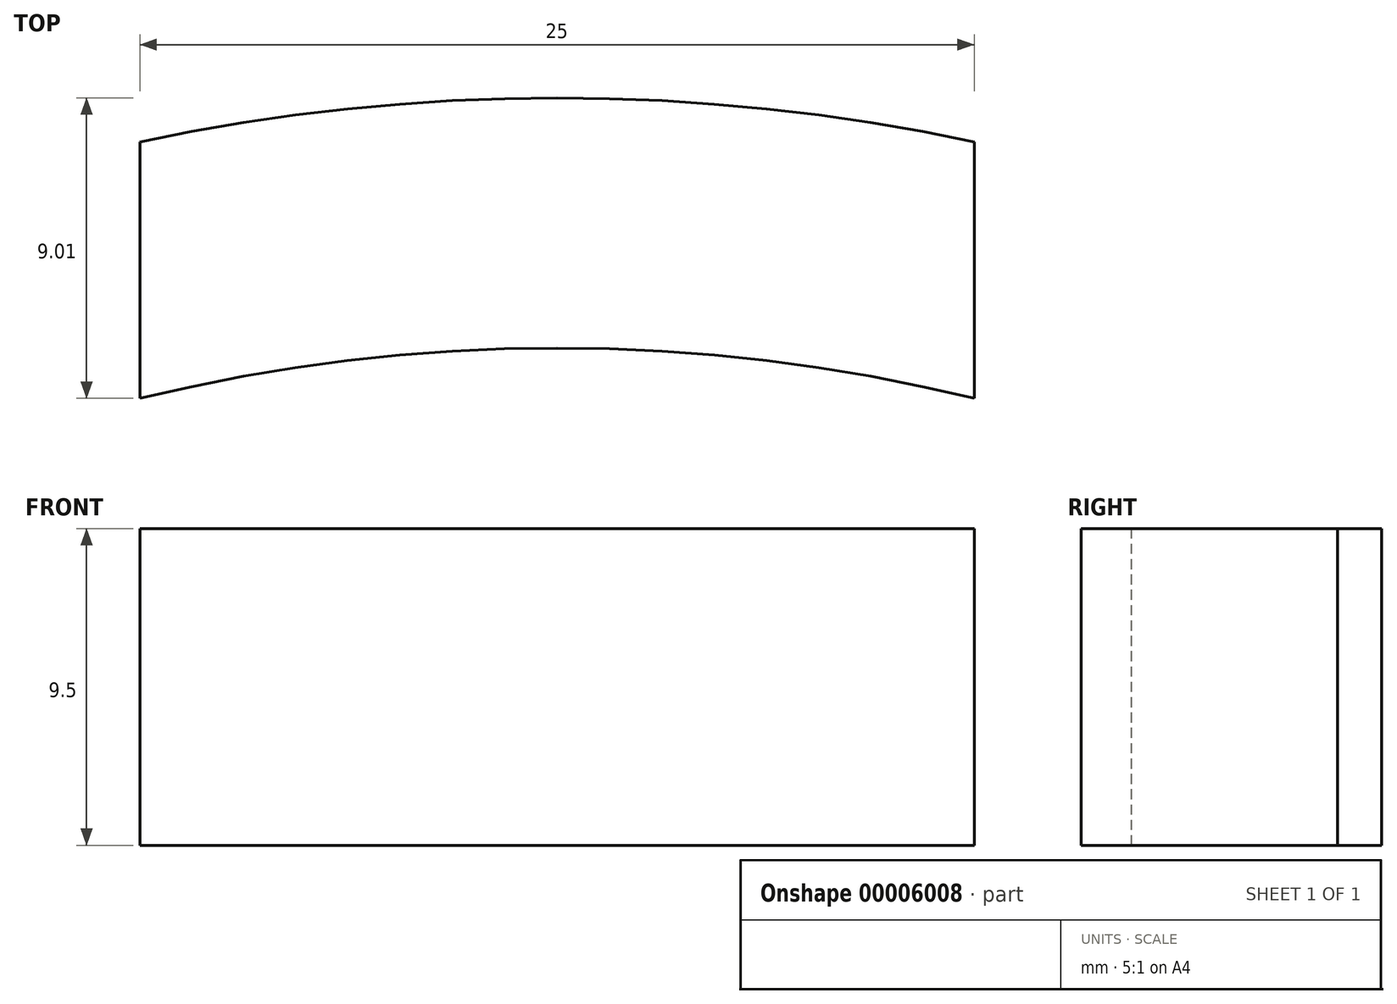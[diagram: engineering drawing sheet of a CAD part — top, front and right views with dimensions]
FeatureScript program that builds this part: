
annotation { "Feature Type Name" : "Feature", "Feature Type Description" : "" }
export const myFeature = defineFeature(function(context is Context, id is Id, definition is map)
    precondition{}
    {
        {
            var Q0;
            Q0=qCreatedBy(makeId("Top.planeOp"),FACE);
            var sketch = newSketch(context, id + "F0", { "sketchPlane" : qUnion([Q0])});
            skCircle(sketch, "E0", {"center": v(0, 0) * mm, "radius": 52.5 * mm});
            skCircle(sketch, "E1", {"center": v(0, 0) * mm, "radius": 60 * mm});
            skLineSegment(sketch, "E2.rect.bottom", {"start": v(12.5, 65.06) * mm, "end": v(-12.5, 65.06) * mm});
            skLineSegment(sketch, "E2.rect.top", {"start": v(12.5, 22.34) * mm, "end": v(-12.5, 22.34) * mm});
            skLineSegment(sketch, "E2.rect.left", {"start": v(12.5, 65.06) * mm, "end": v(12.5, 22.34) * mm});
            skLineSegment(sketch, "E2.rect.right", {"start": v(-12.5, 65.06) * mm, "end": v(-12.5, 22.34) * mm});
            skPoint(sketch, "E2.rect.middle", {"position": v(0, 43.7) * mm});
            skSolve(sketch);
        }
        {
            var Q0;
            {var subQ1=sQuery(id+"F0.wireOp",EDGE,"E0");var subQ5=sQuery(id+"F0.wireOp",EDGE,"E2.rect.left");var subQ7=makeQuery(id+"F0.imprint","INTERSECT",VERTEX,{"derivedFrom":[subQ1,subQ5]});Q0=makeQuery(id+"F0.imprint","IMPRINT",FACE,{"disambiguationData":[TD([[makeQuery(id+"F0.imprint","IMPRINT",EDGE,{"disambiguationData":[TD([[subQ7,-1.0]])],"derivedFrom":subQ1}),-1.0]])]});}
            extrude(context, id + "F1", {"entities" : qUnion([Q0]), "depth" : 9.5 * mm});
        }
    });
